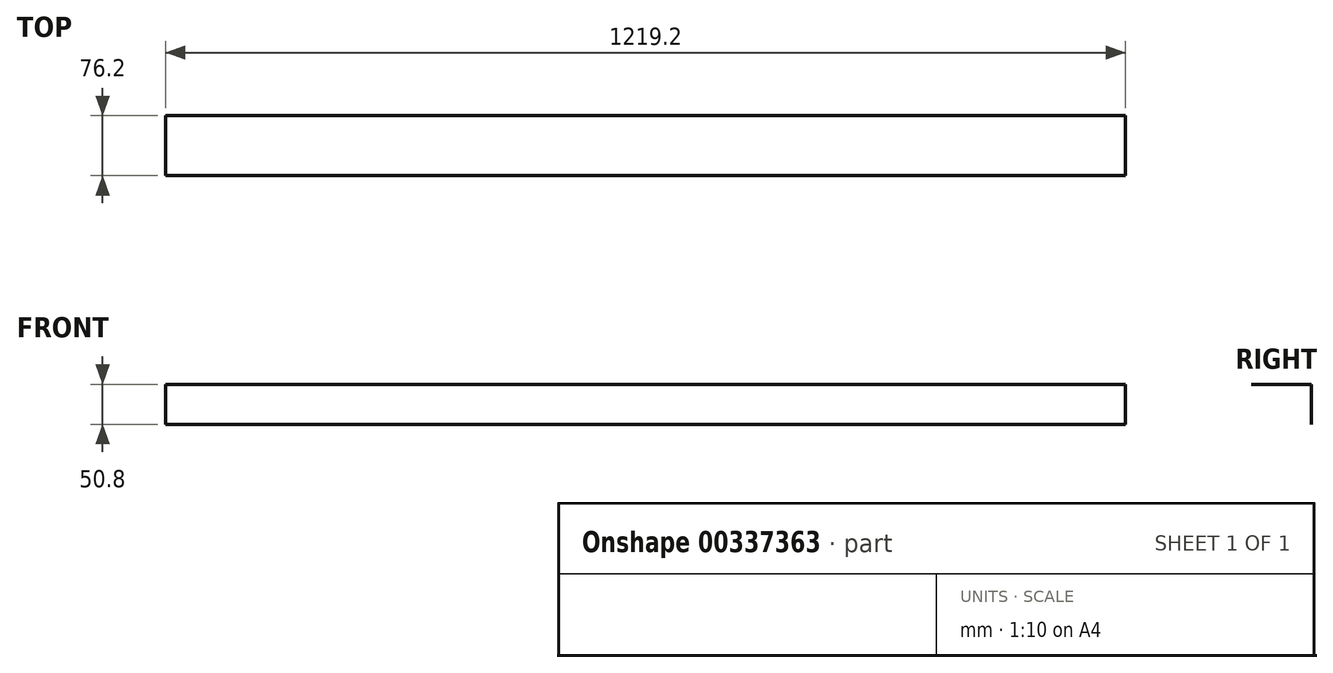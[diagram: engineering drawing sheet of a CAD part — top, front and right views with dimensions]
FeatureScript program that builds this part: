
annotation { "Feature Type Name" : "Feature", "Feature Type Description" : "" }
export const myFeature = defineFeature(function(context is Context, id is Id, definition is map)
    precondition{}
    {
        {
            var Q0;
            Q0=qCreatedBy(makeId("Right.planeOp"),FACE);
            var sketch = newSketch(context, id + "F0", { "sketchPlane" : qUnion([Q0])});
            skLineSegment(sketch, "E0", {"start": v(80.51, -41.35) * mm, "end": v(80.51, 9.45) * mm});
            skLineSegment(sketch, "E1", {"start": v(80.51, 9.45) * mm, "end": v(4.31, 9.45) * mm});
            skSolve(sketch);
        }
        {
            var Q0;
            Q0 = qSketchRegion(id + "F0", true);
            var Q1;
            Q1=sQuery(id+"F0.wireOp",EDGE,"E1");
            var Q2;
            Q2=sQuery(id+"F0.wireOp",EDGE,"E0");
            extrude(context, id + "F1", {"entities" : qUnion([Q0]), "bodyType" : ToolBodyType.SURFACE, "surfaceEntities" : qUnion([Q1, Q2]), "depth" : 1219.2 * mm});
        }
    });
